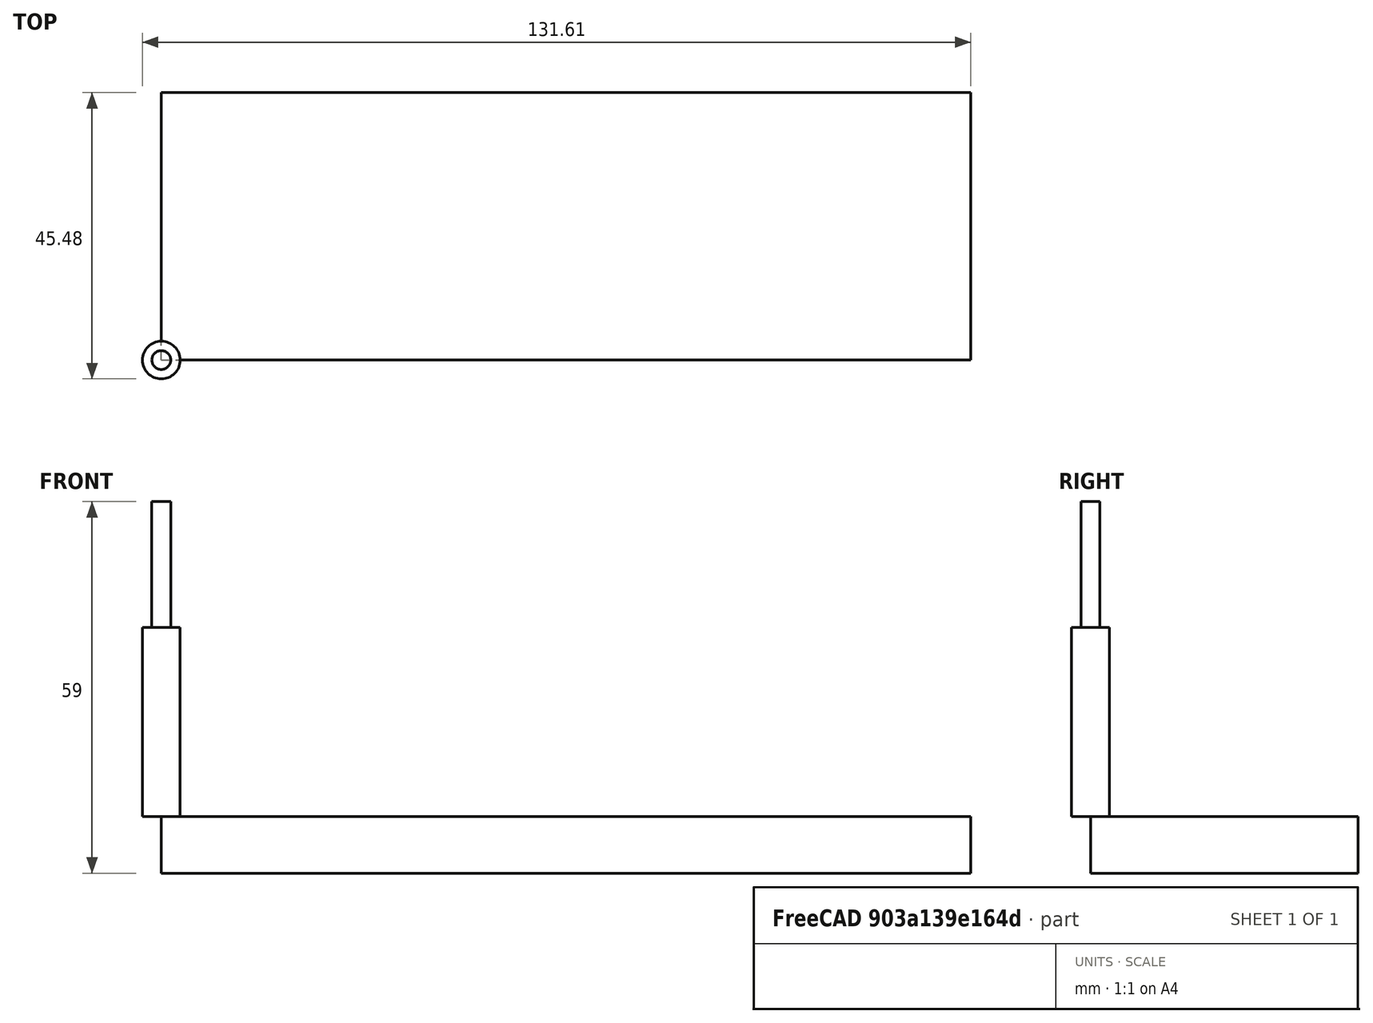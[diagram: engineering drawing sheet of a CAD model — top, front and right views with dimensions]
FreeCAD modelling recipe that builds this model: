
FCSTD DOCUMENT  (FreeCAD 0.19R24276 (Git))
Label: Coinceur2
License: All rights reserved
LicenseURL: http://en.wikipedia.org/wiki/All_rights_reserved
objects: Path::FeaturePython×5, Part::FeaturePython×3, App::DocumentObjectGroup×2, Sketcher::SketchObject×1, PartDesign::Pad×1, PartDesign::Body×1, App::FeaturePython×1, Path::FeatureCompoundPython×1, Mesh::FeaturePython×1
note: 9 computed .brp shape members not serialized (recipe doc carries the construction recipe); baked Part::Feature solids carry a one-line shape summary decoded from their .brp

FEATURE [Sketcher::SketchObject] Sketch002
  FullyConstrained = false
  sketch-geometry (712):
    g0: LineSegment StartX=49.1886 StartY=18.0693 StartZ=0 EndX=51.3408 EndY=18.9617 EndZ=0
    g1: LineSegment StartX=51.3408 StartY=18.9617 StartZ=0 EndX=57.8935 EndY=21.2147 EndZ=0
    g2: LineSegment StartX=57.8935 StartY=21.2147 StartZ=0 EndX=64.573 EndY=23.058 EndZ=0
    g3: LineSegment StartX=64.573 StartY=23.058 StartZ=0 EndX=71.3537 EndY=24.4846 EndZ=0
    g4: LineSegment StartX=71.3537 StartY=24.4846 StartZ=0 EndX=78.2097 EndY=25.4889 EndZ=0
    g5: LineSegment StartX=78.2097 StartY=25.4889 StartZ=0 EndX=85.1148 EndY=26.0672 EndZ=0
    g6: LineSegment StartX=85.1148 StartY=26.0672 StartZ=0 EndX=92.0423 EndY=26.2171 EndZ=0
    g7: LineSegment StartX=92.0423 StartY=26.2171 StartZ=0 EndX=98.9659 EndY=25.9383 EndZ=0
    g8: LineSegment StartX=98.9659 StartY=25.9383 StartZ=0 EndX=105.859 EndY=25.2316 EndZ=0
    g9: LineSegment StartX=105.859 StartY=25.2316 StartZ=0 EndX=112.695 EndY=24.0998 EndZ=0
    g10: LineSegment StartX=112.695 StartY=24.0998 StartZ=0 EndX=119.448 EndY=22.5473 EndZ=0
    g11: LineSegment StartX=119.448 StartY=22.5473 StartZ=0 EndX=126.092 EndY=20.5799 EndZ=0
    g12: LineSegment StartX=126.092 StartY=20.5799 StartZ=0 EndX=126.34 EndY=20.5026 EndZ=0
    g13: LineSegment StartX=126.34 StartY=20.5026 StartZ=0 EndX=126.59 EndY=20.4333 EndZ=0
    g14: LineSegment StartX=126.59 StartY=20.4333 StartZ=0 EndX=126.842 EndY=20.3722 EndZ=0
    g15: LineSegment StartX=126.842 StartY=20.3722 StartZ=0 EndX=127.096 EndY=20.3193 EndZ=0
    g16: LineSegment StartX=127.096 StartY=20.3193 StartZ=0 EndX=127.351 EndY=20.2746 EndZ=0
    g17: LineSegment StartX=127.351 StartY=20.2746 StartZ=0 EndX=127.608 EndY=20.2382 EndZ=0
    g18: LineSegment StartX=127.608 StartY=20.2382 StartZ=0 EndX=127.866 EndY=20.2102 EndZ=0
    g19: LineSegment StartX=127.866 StartY=20.2102 StartZ=0 EndX=128.125 EndY=20.1905 EndZ=0
    g20: LineSegment StartX=128.125 StartY=20.1905 StartZ=0 EndX=128.384 EndY=20.1793 EndZ=0
    g21: LineSegment StartX=128.384 StartY=20.1793 StartZ=0 EndX=128.643 EndY=20.1764 EndZ=0
    g22: LineSegment StartX=128.643 StartY=20.1764 StartZ=0 EndX=128.903 EndY=20.1819 EndZ=0
    g23: LineSegment StartX=128.903 StartY=20.1819 StartZ=0 EndX=129.162 EndY=20.1958 EndZ=0
    g24: LineSegment StartX=129.162 StartY=20.1958 StartZ=0 EndX=129.42 EndY=20.2181 EndZ=0
    g25: LineSegment StartX=129.42 StartY=20.2181 StartZ=0 EndX=129.678 EndY=20.2488 EndZ=0
    g26: LineSegment StartX=129.678 StartY=20.2488 StartZ=0 EndX=129.934 EndY=20.2877 EndZ=0
    g27: LineSegment StartX=129.934 StartY=20.2877 StartZ=0 EndX=130.189 EndY=20.335 EndZ=0
    g28: LineSegment StartX=130.189 StartY=20.335 StartZ=0 EndX=130.443 EndY=20.3905 EndZ=0
    g29: LineSegment StartX=130.443 StartY=20.3905 StartZ=0 EndX=130.694 EndY=20.4542 EndZ=0
    g30: LineSegment StartX=130.694 StartY=20.4542 StartZ=0 EndX=130.944 EndY=20.526 EndZ=0
    g31: LineSegment StartX=130.944 StartY=20.526 StartZ=0 EndX=131.191 EndY=20.6058 EndZ=0
    g32: LineSegment StartX=131.191 StartY=20.6058 StartZ=0 EndX=131.435 EndY=20.6936 EndZ=0
    g33: LineSegment StartX=131.435 StartY=20.6936 StartZ=0 EndX=131.676 EndY=20.7893 EndZ=0
    g34: LineSegment StartX=131.676 StartY=20.7893 StartZ=0 EndX=131.914 EndY=20.8927 EndZ=0
    g35: LineSegment StartX=131.914 StartY=20.8927 StartZ=0 EndX=132.148 EndY=21.0037 EndZ=0
    g36: LineSegment StartX=132.148 StartY=21.0037 StartZ=0 EndX=132.379 EndY=21.1223 EndZ=0
    g37: LineSegment StartX=132.379 StartY=21.1223 StartZ=0 EndX=132.606 EndY=21.2483 EndZ=0
    g38: LineSegment StartX=132.606 StartY=21.2483 StartZ=0 EndX=132.828 EndY=21.3816 EndZ=0
    g39: LineSegment StartX=132.828 StartY=21.3816 StartZ=0 EndX=133.046 EndY=21.522 EndZ=0
    g40: LineSegment StartX=133.046 StartY=21.522 StartZ=0 EndX=133.26 EndY=21.6694 EndZ=0
    g41: LineSegment StartX=133.26 StartY=21.6694 StartZ=0 EndX=133.469 EndY=21.8237 EndZ=0
    g42: LineSegment StartX=133.469 StartY=21.8237 StartZ=0 EndX=133.672 EndY=21.9846 EndZ=0
    g43: LineSegment StartX=133.672 StartY=21.9846 StartZ=0 EndX=133.87 EndY=22.152 EndZ=0
    g44: LineSegment StartX=133.87 StartY=22.152 StartZ=0 EndX=134.063 EndY=22.3258 EndZ=0
    g45: LineSegment StartX=134.063 StartY=22.3258 StartZ=0 EndX=134.25 EndY=22.5057 EndZ=0
    g46: LineSegment StartX=134.25 StartY=22.5057 StartZ=0 EndX=134.431 EndY=22.6915 EndZ=0
    g47: LineSegment StartX=134.431 StartY=22.6915 StartZ=0 EndX=134.606 EndY=22.8831 EndZ=0
    g48: LineSegment StartX=134.606 StartY=22.8831 StartZ=0 EndX=134.774 EndY=23.0803 EndZ=0
    g49: LineSegment StartX=134.774 StartY=23.0803 StartZ=0 EndX=134.936 EndY=23.2829 EndZ=0
    g50: LineSegment StartX=134.936 StartY=23.2829 StartZ=0 EndX=135.092 EndY=23.4906 EndZ=0
    g51: LineSegment StartX=135.092 StartY=23.4906 StartZ=0 EndX=135.24 EndY=23.7032 EndZ=0
    g52: LineSegment StartX=135.24 StartY=23.7032 StartZ=0 EndX=135.382 EndY=23.9205 EndZ=0
    g53: LineSegment StartX=135.382 StartY=23.9205 StartZ=0 EndX=135.517 EndY=24.1423 EndZ=0
    g54: LineSegment StartX=135.517 StartY=24.1423 StartZ=0 EndX=135.644 EndY=24.3683 EndZ=0
    g55: LineSegment StartX=135.644 StartY=24.3683 StartZ=0 EndX=135.764 EndY=24.5984 EndZ=0
    g56: LineSegment StartX=135.764 StartY=24.5984 StartZ=0 EndX=135.876 EndY=24.8322 EndZ=0
    g57: LineSegment StartX=135.876 StartY=24.8322 StartZ=0 EndX=135.981 EndY=25.0695 EndZ=0
    g58: LineSegment StartX=135.981 StartY=25.0695 StartZ=0 EndX=136.078 EndY=25.3101 EndZ=0
    g59: LineSegment StartX=136.078 StartY=25.3101 StartZ=0 EndX=136.167 EndY=25.5537 EndZ=0
    g60: LineSegment StartX=136.167 StartY=25.5537 StartZ=0 EndX=136.249 EndY=25.8001 EndZ=0
    g61: LineSegment StartX=136.249 StartY=25.8001 StartZ=0 EndX=136.322 EndY=26.0489 EndZ=0
    g62: LineSegment StartX=136.322 StartY=26.0489 StartZ=0 EndX=136.387 EndY=26.3 EndZ=0
    g63: LineSegment StartX=136.387 StartY=26.3 StartZ=0 EndX=136.444 EndY=26.5531 EndZ=0
    g64: LineSegment StartX=136.444 StartY=26.5531 StartZ=0 EndX=136.493 EndY=26.8079 EndZ=0
    g65: LineSegment StartX=136.493 StartY=26.8079 StartZ=0 EndX=136.533 EndY=27.0642 EndZ=0
    g66: LineSegment StartX=136.533 StartY=27.0642 StartZ=0 EndX=136.565 EndY=27.3216 EndZ=0
    g67: LineSegment StartX=136.565 StartY=27.3216 StartZ=0 EndX=136.589 EndY=27.5799 EndZ=0
    g68: LineSegment StartX=136.589 StartY=27.5799 StartZ=0 EndX=136.605 EndY=27.8389 EndZ=0
    g69: LineSegment StartX=136.605 StartY=27.8389 StartZ=0 EndX=136.612 EndY=28.0982 EndZ=0
    g70: LineSegment StartX=136.612 StartY=28.0982 StartZ=0 EndX=136.61 EndY=28.3577 EndZ=0
    g71: LineSegment StartX=136.61 StartY=28.3577 StartZ=0 EndX=136.601 EndY=28.6169 EndZ=0
    g72: LineSegment StartX=136.601 StartY=28.6169 StartZ=0 EndX=136.582 EndY=28.8757 EndZ=0
    g73: LineSegment StartX=136.582 StartY=28.8757 StartZ=0 EndX=136.556 EndY=29.1338 EndZ=0
    g74: LineSegment StartX=136.556 StartY=29.1338 StartZ=0 EndX=136.521 EndY=29.3908 EndZ=0
    g75: LineSegment StartX=136.521 StartY=29.3908 StartZ=0 EndX=136.478 EndY=29.6467 EndZ=0
    g76: LineSegment StartX=136.478 StartY=29.6467 StartZ=0 EndX=136.426 EndY=29.9009 EndZ=0
    g77: LineSegment StartX=136.426 StartY=29.9009 StartZ=0 EndX=136.367 EndY=30.1534 EndZ=0
    g78: LineSegment StartX=136.367 StartY=30.1534 StartZ=0 EndX=136.299 EndY=30.4038 EndZ=0
    g79: LineSegment StartX=136.299 StartY=30.4038 StartZ=0 EndX=136.223 EndY=30.6519 EndZ=0
    g80: LineSegment StartX=136.223 StartY=30.6519 StartZ=0 EndX=136.139 EndY=30.8974 EndZ=0
    g81: LineSegment StartX=136.139 StartY=30.8974 StartZ=0 EndX=136.048 EndY=31.1401 EndZ=0
    g82: LineSegment StartX=136.048 StartY=31.1401 StartZ=0 EndX=135.948 EndY=31.3796 EndZ=0
    g83: LineSegment StartX=135.948 StartY=31.3796 StartZ=0 EndX=135.841 EndY=31.6158 EndZ=0
    g84: LineSegment StartX=135.841 StartY=31.6158 StartZ=0 EndX=135.726 EndY=31.8484 EndZ=0
    g85: LineSegment StartX=135.726 StartY=31.8484 StartZ=0 EndX=135.603 EndY=32.0772 EndZ=0
    g86: LineSegment StartX=135.603 StartY=32.0772 StartZ=0 EndX=135.474 EndY=32.3019 EndZ=0
    g87: LineSegment StartX=135.474 StartY=32.3019 StartZ=0 EndX=135.337 EndY=32.5222 EndZ=0
    g88: LineSegment StartX=135.337 StartY=32.5222 StartZ=0 EndX=135.193 EndY=32.738 EndZ=0
    g89: LineSegment StartX=135.193 StartY=32.738 StartZ=0 EndX=135.042 EndY=32.9491 EndZ=0
    g90: LineSegment StartX=135.042 StartY=32.9491 StartZ=0 EndX=134.884 EndY=33.1551 EndZ=0
    g91: LineSegment StartX=134.884 StartY=33.1551 StartZ=0 EndX=134.72 EndY=33.3559 EndZ=0
    g92: LineSegment StartX=134.72 StartY=33.3559 StartZ=0 EndX=134.549 EndY=33.5513 EndZ=0
    g93: LineSegment StartX=134.549 StartY=33.5513 StartZ=0 EndX=134.373 EndY=33.7411 EndZ=0
    g94: LineSegment StartX=134.373 StartY=33.7411 StartZ=0 EndX=134.19 EndY=33.9251 EndZ=0
    g95: LineSegment StartX=134.19 StartY=33.9251 StartZ=0 EndX=134.001 EndY=34.103 EndZ=0
    g96: LineSegment StartX=134.001 StartY=34.103 StartZ=0 EndX=133.806 EndY=34.2747 EndZ=0
    g97: LineSegment StartX=133.806 StartY=34.2747 StartZ=0 EndX=133.606 EndY=34.44 EndZ=0
    g98: LineSegment StartX=133.606 StartY=34.44 StartZ=0 EndX=133.401 EndY=34.5988 EndZ=0
    g99: LineSegment StartX=133.401 StartY=34.5988 StartZ=0 EndX=133.191 EndY=34.7508 EndZ=0
    g100: LineSegment StartX=133.191 StartY=34.7508 StartZ=0 EndX=132.976 EndY=34.896 EndZ=0
    g101: LineSegment StartX=132.976 StartY=34.896 StartZ=0 EndX=132.756 EndY=35.0341 EndZ=0
    g102: LineSegment StartX=132.756 StartY=35.0341 StartZ=0 EndX=132.532 EndY=35.165 EndZ=0
    g103: LineSegment StartX=132.532 StartY=35.165 StartZ=0 EndX=132.304 EndY=35.2886 EndZ=0
    g104: LineSegment StartX=132.304 StartY=35.2886 StartZ=0 EndX=132.072 EndY=35.4048 EndZ=0
    g105: LineSegment StartX=132.072 StartY=35.4048 StartZ=0 EndX=131.837 EndY=35.5134 EndZ=0
    g106: LineSegment StartX=131.837 StartY=35.5134 StartZ=0 EndX=131.598 EndY=35.6143 EndZ=0
    g107: LineSegment StartX=131.598 StartY=35.6143 StartZ=0 EndX=131.356 EndY=35.7074 EndZ=0
    g108: LineSegment StartX=131.356 StartY=35.7074 StartZ=0 EndX=131.111 EndY=35.7926 EndZ=0
    g109: LineSegment StartX=131.111 StartY=35.7926 StartZ=0 EndX=130.863 EndY=35.8698 EndZ=0
    g110: LineSegment StartX=130.863 StartY=35.8698 StartZ=0 EndX=130.613 EndY=36 EndZ=0
    g111: LineSegment StartX=130.613 StartY=36 StartZ=0 EndX=130.361 EndY=36 EndZ=0
    g112: LineSegment StartX=130.361 StartY=36 StartZ=0 EndX=129.386 EndY=36.2768 EndZ=0
    g113: LineSegment StartX=129.386 StartY=36.2768 StartZ=0 EndX=128.411 EndY=36.551 EndZ=0
    g114: LineSegment StartX=128.411 StartY=36.551 StartZ=0 EndX=127.435 EndY=36.8224 EndZ=0
    g115: LineSegment StartX=127.435 StartY=36.8224 StartZ=0 EndX=126.458 EndY=37.0911 EndZ=0
    g116: LineSegment StartX=126.458 StartY=37.0911 StartZ=0 EndX=125.481 EndY=37.357 EndZ=0
    g117: LineSegment StartX=125.481 StartY=37.357 StartZ=0 EndX=124.503 EndY=37.6203 EndZ=0
    g118: LineSegment StartX=124.503 StartY=37.6203 StartZ=0 EndX=123.524 EndY=37.8808 EndZ=0
    g119: LineSegment StartX=123.524 StartY=37.8808 StartZ=0 EndX=122.544 EndY=38.1386 EndZ=0
    g120: LineSegment StartX=122.544 StartY=38.1386 StartZ=0 EndX=121.564 EndY=38.3937 EndZ=0
    g121: LineSegment StartX=121.564 StartY=38.3937 StartZ=0 EndX=120.583 EndY=38.6461 EndZ=0
    g122: LineSegment StartX=120.583 StartY=38.6461 StartZ=0 EndX=119.601 EndY=38.8957 EndZ=0
    g123: LineSegment StartX=119.601 StartY=38.8957 StartZ=0 EndX=118.618 EndY=39.1426 EndZ=0
    g124: LineSegment StartX=118.618 StartY=39.1426 StartZ=0 EndX=117.635 EndY=39.3868 EndZ=0
    g125: LineSegment StartX=117.635 StartY=39.3868 StartZ=0 EndX=116.651 EndY=39.6282 EndZ=0
    g126: LineSegment StartX=116.651 StartY=39.6282 StartZ=0 EndX=115.667 EndY=39.8669 EndZ=0
    g127: LineSegment StartX=115.667 StartY=39.8669 StartZ=0 EndX=114.682 EndY=40.1028 EndZ=0
    g128: LineSegment StartX=114.682 StartY=40.1028 StartZ=0 EndX=113.696 EndY=40.336 EndZ=0
    g129: LineSegment StartX=113.696 StartY=40.336 StartZ=0 EndX=112.709 EndY=40.5665 EndZ=0
    g130: LineSegment StartX=112.709 StartY=40.5665 StartZ=0 EndX=111.722 EndY=40.7942 EndZ=0
    g131: LineSegment StartX=111.722 StartY=40.7942 StartZ=0 EndX=110.735 EndY=41.0192 EndZ=0
    g132: LineSegment StartX=110.735 StartY=41.0192 StartZ=0 EndX=109.746 EndY=41.2414 EndZ=0
    g133: LineSegment StartX=109.746 StartY=41.2414 StartZ=0 EndX=108.757 EndY=41.4608 EndZ=0
    g134: LineSegment StartX=108.757 StartY=41.4608 StartZ=0 EndX=107.768 EndY=41.6776 EndZ=0
    g135: LineSegment StartX=107.768 StartY=41.6776 StartZ=0 EndX=106.778 EndY=41.8915 EndZ=0
    g136: LineSegment StartX=106.778 StartY=41.8915 StartZ=0 EndX=105.787 EndY=42.1027 EndZ=0
    g137: LineSegment StartX=105.787 StartY=42.1027 StartZ=0 EndX=104.796 EndY=42.3112 EndZ=0
    g138: LineSegment StartX=104.796 StartY=42.3112 StartZ=0 EndX=103.804 EndY=42.5169 EndZ=0
    g139: LineSegment StartX=103.804 StartY=42.5169 StartZ=0 EndX=102.811 EndY=42.7198 EndZ=0
    g140: LineSegment StartX=102.811 StartY=42.7198 StartZ=0 EndX=101.818 EndY=42.92 EndZ=0
    g141: LineSegment StartX=101.818 StartY=42.92 StartZ=0 EndX=100.825 EndY=43.1174 EndZ=0
    g142: LineSegment StartX=100.825 StartY=43.1174 StartZ=0 EndX=99.8304 EndY=43.312 EndZ=0
    g143: LineSegment StartX=99.8304 StartY=43.312 StartZ=0 EndX=98.8357 EndY=43.5039 EndZ=0
    g144: LineSegment StartX=98.8357 StartY=43.5039 StartZ=0 EndX=97.8405 EndY=43.693 EndZ=0
    g145: LineSegment StartX=97.8405 StartY=43.693 StartZ=0 EndX=96.8448 EndY=43.8793 EndZ=0
    g146: LineSegment StartX=96.8448 StartY=43.8793 StartZ=0 EndX=95.8485 EndY=44.0629 EndZ=0
    g147: LineSegment StartX=95.8485 StartY=44.0629 StartZ=0 EndX=94.8518 EndY=44.2437 EndZ=0
    g148: LineSegment StartX=94.8518 StartY=44.2437 StartZ=0 EndX=93.8545 EndY=44.4217 EndZ=0
    g149: LineSegment StartX=93.8545 StartY=44.4217 StartZ=0 EndX=92.8568 EndY=44.597 EndZ=0
    g150: LineSegment StartX=92.8568 StartY=44.597 StartZ=0 EndX=91.8585 EndY=44.7694 EndZ=0
    g151: LineSegment StartX=91.8585 StartY=44.7694 StartZ=0 EndX=90.8598 EndY=44.9391 EndZ=0
    g152: LineSegment StartX=90.8598 StartY=44.9391 StartZ=0 EndX=89.8607 EndY=45.1061 EndZ=0
    g153: LineSegment StartX=89.8607 StartY=45.1061 StartZ=0 EndX=88.861 EndY=45.2702 EndZ=0
    g154: LineSegment StartX=88.861 StartY=45.2702 StartZ=0 EndX=87.861 EndY=45.4315 EndZ=0
    g155: LineSegment StartX=87.861 StartY=45.4315 StartZ=0 EndX=86.8604 EndY=45.5901 EndZ=0
    g156: LineSegment StartX=86.8604 StartY=45.5901 StartZ=0 EndX=85.8595 EndY=45.7459 EndZ=0
    g157: LineSegment StartX=85.8595 StartY=45.7459 StartZ=0 EndX=84.8581 EndY=45.8989 EndZ=0
    g158: LineSegment StartX=84.8581 StartY=45.8989 StartZ=0 EndX=83.8563 EndY=46.0491 EndZ=0
    g159: LineSegment StartX=83.8563 StartY=46.0491 StartZ=0 EndX=82.854 EndY=46.1965 EndZ=0
    g160: LineSegment StartX=82.854 StartY=46.1965 StartZ=0 EndX=81.8514 EndY=46.3412 EndZ=0
    g161: LineSegment StartX=81.8514 StartY=46.3412 StartZ=0 EndX=80.8483 EndY=46.483 EndZ=0
    g162: LineSegment StartX=80.8483 StartY=46.483 StartZ=0 EndX=79.8449 EndY=46.6221 EndZ=0
    g163: LineSegment StartX=79.8449 StartY=46.6221 StartZ=0 EndX=78.8411 EndY=46.7583 EndZ=0
    g164: LineSegment StartX=78.8411 StartY=46.7583 StartZ=0 EndX=77.8369 EndY=46.8918 EndZ=0
    g165: LineSegment StartX=77.8369 StartY=46.8918 StartZ=0 EndX=76.8324 EndY=47.0225 EndZ=0
    g166: LineSegment StartX=76.8324 StartY=47.0225 StartZ=0 EndX=75.8275 EndY=47.1504 EndZ=0
    g167: LineSegment StartX=75.8275 StartY=47.1504 StartZ=0 EndX=74.8222 EndY=47.2755 EndZ=0
    g168: LineSegment StartX=74.8222 StartY=47.2755 StartZ=0 EndX=73.8166 EndY=47.3977 EndZ=0
    g169: LineSegment StartX=73.8166 StartY=47.3977 StartZ=0 EndX=72.8107 EndY=47.5172 EndZ=0
    g170: LineSegment StartX=72.8107 StartY=47.5172 StartZ=0 EndX=71.8044 EndY=47.6339 EndZ=0
    g171: LineSegment StartX=71.8044 StartY=47.6339 StartZ=0 EndX=70.7978 EndY=47.7478 EndZ=0
    g172: LineSegment StartX=70.7978 StartY=47.7478 StartZ=0 EndX=69.7909 EndY=47.8589 EndZ=0
    g173: LineSegment StartX=69.7909 StartY=47.8589 StartZ=0 EndX=68.7837 EndY=47.9672 EndZ=0
    g174: LineSegment StartX=68.7837 StartY=47.9672 StartZ=0 EndX=67.7762 EndY=48.0727 EndZ=0
    g175: LineSegment StartX=67.7762 StartY=48.0727 StartZ=0 EndX=66.7684 EndY=48.1754 EndZ=0
    g176: LineSegment StartX=66.7684 StartY=48.1754 StartZ=0 EndX=65.7603 EndY=48.2753 EndZ=0
    g177: LineSegment StartX=65.7603 StartY=48.2753 StartZ=0 EndX=64.7519 EndY=48.3723 EndZ=0
    g178: LineSegment StartX=64.7519 StartY=48.3723 StartZ=0 EndX=63.7433 EndY=48.4666 EndZ=0
    g179: LineSegment StartX=63.7433 StartY=48.4666 StartZ=0 EndX=62.7344 EndY=48.5581 EndZ=0
    g180: LineSegment StartX=62.7344 StartY=48.5581 StartZ=0 EndX=61.7253 EndY=48.6467 EndZ=0
    g181: LineSegment StartX=61.7253 StartY=48.6467 StartZ=0 EndX=60.7159 EndY=48.7326 EndZ=0
    g182: LineSegment StartX=60.7159 StartY=48.7326 StartZ=0 EndX=59.7063 EndY=48.8156 EndZ=0
    g183: LineSegment StartX=59.7063 StartY=48.8156 StartZ=0 EndX=58.6965 EndY=48.8959 EndZ=0
    g184: LineSegment StartX=58.6965 StartY=48.8959 StartZ=0 EndX=57.6864 EndY=48.9733 EndZ=0
    g185: LineSegment StartX=57.6864 StartY=48.9733 StartZ=0 EndX=56.6762 EndY=49.0479 EndZ=0
    g186: LineSegment StartX=56.6762 StartY=49.0479 StartZ=0 EndX=55.6657 EndY=49.1197 EndZ=0
    g187: LineSegment StartX=55.6657 StartY=49.1197 StartZ=0 EndX=54.655 EndY=49.1887 EndZ=0
    g188: LineSegment StartX=54.655 StartY=49.1887 StartZ=0 EndX=53.6442 EndY=49.2549 EndZ=0
    g189: LineSegment StartX=53.6442 StartY=49.2549 StartZ=0 EndX=52.6332 EndY=49.3182 EndZ=0
    g190: LineSegment StartX=52.6332 StartY=49.3182 StartZ=0 EndX=51.622 EndY=49.3788 EndZ=0
    g191: LineSegment StartX=51.622 StartY=49.3788 StartZ=0 EndX=50.6106 EndY=49.4365 EndZ=0
    g192: LineSegment StartX=50.6106 StartY=49.4365 StartZ=0 EndX=49.5991 EndY=49.4914 EndZ=0
    g193: LineSegment StartX=49.5991 StartY=49.4914 StartZ=0 EndX=48.5874 EndY=49.5436 EndZ=0
    g194: LineSegment StartX=48.5874 StartY=49.5436 StartZ=0 EndX=47.5756 EndY=49.5929 EndZ=0
    g195: LineSegment StartX=47.5756 StartY=49.5929 StartZ=0 EndX=46.5636 EndY=49.6393 EndZ=0
    g196: LineSegment StartX=46.5636 StartY=49.6393 StartZ=0 EndX=45.5516 EndY=49.683 EndZ=0
    g197: LineSegment StartX=45.5516 StartY=49.683 StartZ=0 EndX=44.5394 EndY=49.7239 EndZ=0
    g198: LineSegment StartX=44.5394 StartY=49.7239 StartZ=0 EndX=43.5271 EndY=49.7619 EndZ=0
    g199: LineSegment StartX=43.5271 StartY=49.7619 StartZ=0 EndX=42.5147 EndY=49.7971 EndZ=0
    g200: LineSegment StartX=42.5147 StartY=49.7971 StartZ=0 EndX=41.5022 EndY=49.8295 EndZ=0
    g201: LineSegment StartX=41.5022 StartY=49.8295 StartZ=0 EndX=40.4896 EndY=49.8591 EndZ=0
    g202: LineSegment StartX=40.4896 StartY=49.8591 StartZ=0 EndX=39.4769 EndY=49.8859 EndZ=0
    g203: LineSegment StartX=39.4769 StartY=49.8859 StartZ=0 EndX=38.4642 EndY=49.9098 EndZ=0
    g204: LineSegment StartX=38.4642 StartY=49.9098 StartZ=0 EndX=37.4514 EndY=49.931 EndZ=0
    g205: LineSegment StartX=37.4514 StartY=49.931 StartZ=0 EndX=36.4385 EndY=49.9493 EndZ=0
    g206: LineSegment StartX=36.4385 StartY=49.9493 StartZ=0 EndX=35.4256 EndY=49.9648 EndZ=0
    g207: LineSegment StartX=35.4256 StartY=49.9648 StartZ=0 EndX=34.4127 EndY=49.9775 EndZ=0
    g208: LineSegment StartX=34.4127 StartY=49.9775 StartZ=0 EndX=33.3997 EndY=49.9873 EndZ=0
    g209: LineSegment StartX=33.3997 StartY=49.9873 StartZ=0 EndX=32.3867 EndY=49.9944 EndZ=0
    g210: LineSegment StartX=32.3867 StartY=49.9944 StartZ=0 EndX=30.3607 EndY=49.9895 EndZ=0
    g211: LineSegment StartX=30.3607 StartY=49.9895 StartZ=0 EndX=30.2393 EndY=50.0208 EndZ=0
    g212: LineSegment StartX=30.2393 StartY=50.0208 StartZ=0 EndX=30.1176 EndY=50.0511 EndZ=0
    g213: LineSegment StartX=30.1176 StartY=50.0511 StartZ=0 EndX=29.9957 EndY=50.0804 EndZ=0
    g214: LineSegment StartX=29.9957 StartY=50.0804 StartZ=0 EndX=29.8735 EndY=50.1087 EndZ=0
    g215: LineSegment StartX=29.8735 StartY=50.1087 StartZ=0 EndX=29.7511 EndY=50.1359 EndZ=0
    g216: LineSegment StartX=29.7511 StartY=50.1359 StartZ=0 EndX=29.6284 EndY=50.1621 EndZ=0
    g217: LineSegment StartX=29.6284 StartY=50.1621 StartZ=0 EndX=29.5056 EndY=50.1873 EndZ=0
    g218: LineSegment StartX=29.5056 StartY=50.1873 StartZ=0 EndX=29.3825 EndY=50.2114 EndZ=0
    g219: LineSegment StartX=29.3825 StartY=50.2114 StartZ=0 EndX=29.2593 EndY=50.2345 EndZ=0
    g220: LineSegment StartX=29.2593 StartY=50.2345 StartZ=0 EndX=29.1359 EndY=50.2566 EndZ=0
    g221: LineSegment StartX=29.1359 StartY=50.2566 StartZ=0 EndX=29.0122 EndY=50.2777 EndZ=0
    g222: LineSegment StartX=29.0122 StartY=50.2777 StartZ=0 EndX=28.8884 EndY=50.2977 EndZ=0
    g223: LineSegment StartX=28.8884 StartY=50.2977 StartZ=0 EndX=28.7645 EndY=50.3167 EndZ=0
    g224: LineSegment StartX=28.7645 StartY=50.3167 StartZ=0 EndX=28.6404 EndY=50.3346 EndZ=0
    g225: LineSegment StartX=28.6404 StartY=50.3346 StartZ=0 EndX=28.5161 EndY=50.3516 EndZ=0
    g226: LineSegment StartX=28.5161 StartY=50.3516 StartZ=0 EndX=28.3917 EndY=50.3674 EndZ=0
    g227: LineSegment StartX=28.3917 StartY=50.3674 StartZ=0 EndX=28.2672 EndY=50.3823 EndZ=0
    g228: LineSegment StartX=28.2672 StartY=50.3823 StartZ=0 EndX=28.1426 EndY=50.396 EndZ=0
    g229: LineSegment StartX=28.1426 StartY=50.396 StartZ=0 EndX=28.0178 EndY=50.4088 EndZ=0
    g230: LineSegment StartX=28.0178 StartY=50.4088 StartZ=0 EndX=27.893 EndY=50.4205 EndZ=0
    g231: LineSegment StartX=27.893 StartY=50.4205 StartZ=0 EndX=27.768 EndY=50.4312 EndZ=0
    g232: LineSegment StartX=27.768 StartY=50.4312 StartZ=0 EndX=27.643 EndY=50.4408 EndZ=0
    g233: LineSegment StartX=27.643 StartY=50.4408 StartZ=0 EndX=27.5179 EndY=50.4493 EndZ=0
    g234: LineSegment StartX=27.5179 StartY=50.4493 StartZ=0 EndX=27.3927 EndY=50.4569 EndZ=0
    g235: LineSegment StartX=27.3927 StartY=50.4569 StartZ=0 EndX=27.2675 EndY=50.4633 EndZ=0
    g236: LineSegment StartX=27.2675 StartY=50.4633 StartZ=0 EndX=27.1422 EndY=50.4688 EndZ=0
    g237: LineSegment StartX=27.1422 StartY=50.4688 StartZ=0 EndX=27.0169 EndY=50.4732 EndZ=0
    g238: LineSegment StartX=27.0169 StartY=50.4732 StartZ=0 EndX=26.8915 EndY=50.4765 EndZ=0
    g239: LineSegment StartX=26.8915 StartY=50.4765 StartZ=0 EndX=26.7661 EndY=50.4788 EndZ=0
    g240: LineSegment StartX=26.7661 StartY=50.4788 StartZ=0 EndX=26.6407 EndY=50.48 EndZ=0
    g241: LineSegment StartX=26.6407 StartY=50.48 StartZ=0 EndX=26.5153 EndY=50.4802 EndZ=0
    g242: LineSegment StartX=26.5153 StartY=50.4802 StartZ=0 EndX=26.3899 EndY=50.4793 EndZ=0
    g243: LineSegment StartX=26.3899 StartY=50.4793 StartZ=0 EndX=26.2645 EndY=50.4774 EndZ=0
    g244: LineSegment StartX=26.2645 StartY=50.4774 StartZ=0 EndX=26.1392 EndY=50.4745 EndZ=0
    g245: LineSegment StartX=26.1392 StartY=50.4745 StartZ=0 EndX=26.0138 EndY=50.4705 EndZ=0
    g246: LineSegment StartX=26.0138 StartY=50.4705 StartZ=0 EndX=25.8885 EndY=50.4654 EndZ=0
    g247: LineSegment StartX=25.8885 StartY=50.4654 StartZ=0 EndX=25.7633 EndY=50.4593 EndZ=0
    g248: LineSegment StartX=25.7633 StartY=50.4593 StartZ=0 EndX=25.6381 EndY=50.4522 EndZ=0
    g249: LineSegment StartX=25.6381 StartY=50.4522 StartZ=0 EndX=25.5129 EndY=50.444 EndZ=0
    g250: LineSegment StartX=25.5129 StartY=50.444 StartZ=0 EndX=25.3879 EndY=50.4348 EndZ=0
    g251: LineSegment StartX=25.3879 StartY=50.4348 StartZ=0 EndX=25.2629 EndY=50.4245 EndZ=0
    g252: LineSegment StartX=25.2629 StartY=50.4245 StartZ=0 EndX=25.138 EndY=50.4131 EndZ=0
    g253: LineSegment StartX=25.138 StartY=50.4131 StartZ=0 EndX=25.0132 EndY=50.4008 EndZ=0
    g254: LineSegment StartX=25.0132 StartY=50.4008 StartZ=0 EndX=24.8885 EndY=50.3874 EndZ=0
    g255: LineSegment StartX=24.8885 StartY=50.3874 StartZ=0 EndX=24.764 EndY=50.3729 EndZ=0
    g256: LineSegment StartX=24.764 StartY=50.3729 StartZ=0 EndX=24.6395 EndY=50.3574 EndZ=0
    g257: LineSegment StartX=24.6395 StartY=50.3574 StartZ=0 EndX=24.5152 EndY=50.3409 EndZ=0
    g258: LineSegment StartX=24.5152 StartY=50.3409 StartZ=0 EndX=24.3911 EndY=50.3233 EndZ=0
    g259: LineSegment StartX=24.3911 StartY=50.3233 StartZ=0 EndX=24.2671 EndY=50.3047 EndZ=0
    g260: LineSegment StartX=24.2671 StartY=50.3047 StartZ=0 EndX=24.1432 EndY=50.285 EndZ=0
    g261: LineSegment StartX=24.1432 StartY=50.285 StartZ=0 EndX=24.0195 EndY=50.2644 EndZ=0
    g262: LineSegment StartX=24.0195 StartY=50.2644 StartZ=0 EndX=23.896 EndY=50.2426 EndZ=0
    g263: LineSegment StartX=23.896 StartY=50.2426 StartZ=0 EndX=23.7727 EndY=50.2199 EndZ=0
    g264: LineSegment StartX=23.7727 StartY=50.2199 StartZ=0 EndX=23.6496 EndY=50.1961 EndZ=0
    g265: LineSegment StartX=23.6496 StartY=50.1961 StartZ=0 EndX=23.5266 EndY=50.1713 EndZ=0
    g266: LineSegment StartX=23.5266 StartY=50.1713 StartZ=0 EndX=23.4039 EndY=50.1455 EndZ=0
    g267: LineSegment StartX=23.4039 StartY=50.1455 StartZ=0 EndX=23.2814 EndY=50.1186 EndZ=0
    g268: LineSegment StartX=23.2814 StartY=50.1186 StartZ=0 EndX=23.1592 EndY=50.0907 EndZ=0
    g269: LineSegment StartX=23.1592 StartY=50.0907 StartZ=0 EndX=23.0371 EndY=50.0618 EndZ=0
    g270: LineSegment StartX=23.0371 StartY=50.0618 StartZ=0 EndX=22.9154 EndY=50.0319 EndZ=0
    g271: LineSegment StartX=22.9154 StartY=50.0319 StartZ=0 EndX=22.7938 EndY=50.001 EndZ=0
    g272: LineSegment StartX=22.7938 StartY=50.001 StartZ=0 EndX=22.6726 EndY=49.969 EndZ=0
    g273: LineSegment StartX=22.6726 StartY=49.969 StartZ=0 EndX=22.5516 EndY=49.9361 EndZ=0
    g274: LineSegment StartX=22.5516 StartY=49.9361 StartZ=0 EndX=22.4309 EndY=49.9021 EndZ=0
    g275: LineSegment StartX=22.4309 StartY=49.9021 StartZ=0 EndX=22.3105 EndY=49.8671 EndZ=0
    g276: LineSegment StartX=22.3105 StartY=49.8671 StartZ=0 EndX=22.1903 EndY=49.8311 EndZ=0
    g277: LineSegment StartX=22.1903 StartY=49.8311 StartZ=0 EndX=22.0705 EndY=49.7941 EndZ=0
    g278: LineSegment StartX=22.0705 StartY=49.7941 StartZ=0 EndX=21.951 EndY=49.7561 EndZ=0
    g279: LineSegment StartX=21.951 StartY=49.7561 StartZ=0 EndX=21.8318 EndY=49.7171 EndZ=0
    g280: LineSegment StartX=21.8318 StartY=49.7171 StartZ=0 EndX=21.713 EndY=49.6771 EndZ=0
    g281: LineSegment StartX=21.713 StartY=49.6771 StartZ=0 EndX=21.5944 EndY=49.6362 EndZ=0
    g282: LineSegment StartX=21.5944 StartY=49.6362 StartZ=0 EndX=21.4763 EndY=49.5942 EndZ=0
    g283: LineSegment StartX=21.4763 StartY=49.5942 StartZ=0 EndX=21.3585 EndY=49.5512 EndZ=0
    g284: LineSegment StartX=21.3585 StartY=49.5512 StartZ=0 EndX=21.241 EndY=49.5073 EndZ=0
    g285: LineSegment StartX=21.241 StartY=49.5073 StartZ=0 EndX=21.1239 EndY=49.4624 EndZ=0
    g286: LineSegment StartX=21.1239 StartY=49.4624 StartZ=0 EndX=21.0072 EndY=49.4165 EndZ=0
    g287: LineSegment StartX=21.0072 StartY=49.4165 StartZ=0 EndX=20.8909 EndY=49.3696 EndZ=0
    g288: LineSegment StartX=20.8909 StartY=49.3696 StartZ=0 EndX=20.775 EndY=49.3218 EndZ=0
    g289: LineSegment StartX=20.775 StartY=49.3218 StartZ=0 EndX=20.6595 EndY=49.273 EndZ=0
    g290: LineSegment StartX=20.6595 StartY=49.273 StartZ=0 EndX=20.5444 EndY=49.2232 EndZ=0
    g291: LineSegment StartX=20.5444 StartY=49.2232 StartZ=0 EndX=20.4297 EndY=49.1725 EndZ=0
    g292: LineSegment StartX=20.4297 StartY=49.1725 StartZ=0 EndX=20.3154 EndY=49.1208 EndZ=0
    g293: LineSegment StartX=20.3154 StartY=49.1208 StartZ=0 EndX=20.2016 EndY=49.0681 EndZ=0
    g294: LineSegment StartX=20.2016 StartY=49.0681 StartZ=0 EndX=20.0883 EndY=49.0145 EndZ=0
    g295: LineSegment StartX=20.0883 StartY=49.0145 StartZ=0 EndX=19.9753 EndY=48.96 EndZ=0
    g296: LineSegment StartX=19.9753 StartY=48.96 StartZ=0 EndX=19.8629 EndY=48.9045 EndZ=0
    g297: LineSegment StartX=19.8629 StartY=48.9045 StartZ=0 EndX=19.7509 EndY=48.8481 EndZ=0
    g298: LineSegment StartX=19.7509 StartY=48.8481 StartZ=0 EndX=19.6394 EndY=48.7907 EndZ=0
    g299: LineSegment StartX=19.6394 StartY=48.7907 StartZ=0 EndX=19.5283 EndY=48.7325 EndZ=0
    g300: LineSegment StartX=19.5283 StartY=48.7325 StartZ=0 EndX=19.4178 EndY=48.6733 EndZ=0
    g301: LineSegment StartX=19.4178 StartY=48.6733 StartZ=0 EndX=19.3077 EndY=48.6131 EndZ=0
    g302: LineSegment StartX=19.3077 StartY=48.6131 StartZ=0 EndX=19.1982 EndY=48.5521 EndZ=0
    g303: LineSegment StartX=19.1982 StartY=48.5521 StartZ=0 EndX=19.0892 EndY=48.4901 EndZ=0
    g304: LineSegment StartX=19.0892 StartY=48.4901 StartZ=0 EndX=18.9807 EndY=48.4272 EndZ=0
    g305: LineSegment StartX=18.9807 StartY=48.4272 StartZ=0 EndX=18.8727 EndY=48.3635 EndZ=0
    g306: LineSegment StartX=18.8727 StartY=48.3635 StartZ=0 EndX=18.7653 EndY=48.2988 EndZ=0
    g307: LineSegment StartX=18.7653 StartY=48.2988 StartZ=0 EndX=18.6584 EndY=48.2332 EndZ=0
    g308: LineSegment StartX=18.6584 StartY=48.2332 StartZ=0 EndX=18.552 EndY=48.1667 EndZ=0
    g309: LineSegment StartX=18.552 StartY=48.1667 StartZ=0 EndX=18.4463 EndY=48.0994 EndZ=0
    g310: LineSegment StartX=18.4463 StartY=48.0994 StartZ=0 EndX=18.341 EndY=48.0312 EndZ=0
    g311: LineSegment StartX=18.341 StartY=48.0312 StartZ=0 EndX=18.2164 EndY=47.9503 EndZ=0
    g312: LineSegment StartX=18.2164 StartY=47.9503 StartZ=0 EndX=18.0924 EndY=47.8684 EndZ=0
    g313: LineSegment StartX=18.0924 StartY=47.8684 StartZ=0 EndX=17.9691 EndY=47.7855 EndZ=0
    g314: LineSegment StartX=17.9691 StartY=47.7855 StartZ=0 EndX=17.8464 EndY=47.7016 EndZ=0
    g315: LineSegment StartX=17.8464 StartY=47.7016 StartZ=0 EndX=17.7245 EndY=47.6166 EndZ=0
    g316: LineSegment StartX=17.7245 StartY=47.6166 StartZ=0 EndX=17.6033 EndY=47.5307 EndZ=0
    g317: LineSegment StartX=17.6033 StartY=47.5307 StartZ=0 EndX=17.4828 EndY=47.4438 EndZ=0
    g318: LineSegment StartX=17.4828 StartY=47.4438 StartZ=0 EndX=17.363 EndY=47.3558 EndZ=0
    g319: LineSegment StartX=17.363 StartY=47.3558 StartZ=0 EndX=17.2439 EndY=47.2669 EndZ=0
    g320: LineSegment StartX=17.2439 StartY=47.2669 StartZ=0 EndX=17.1256 EndY=47.177 EndZ=0
    g321: LineSegment StartX=17.1256 StartY=47.177 StartZ=0 EndX=17.008 EndY=47.0862 EndZ=0
    g322: LineSegment StartX=17.008 StartY=47.0862 StartZ=0 EndX=16.8912 EndY=46.9943 EndZ=0
    g323: LineSegment StartX=16.8912 StartY=46.9943 StartZ=0 EndX=16.7751 EndY=46.9015 EndZ=0
    g324: LineSegment StartX=16.7751 StartY=46.9015 StartZ=0 EndX=16.6599 EndY=46.8078 EndZ=0
    g325: LineSegment StartX=16.6599 StartY=46.8078 StartZ=0 EndX=16.5453 EndY=46.7131 EndZ=0
    g326: LineSegment StartX=16.5453 StartY=46.7131 StartZ=0 EndX=16.4316 EndY=46.6174 EndZ=0
    g327: LineSegment StartX=16.4316 StartY=46.6174 StartZ=0 EndX=16.3187 EndY=46.5208 EndZ=0
    g328: LineSegment StartX=16.3187 StartY=46.5208 StartZ=0 EndX=16.2066 EndY=46.4233 EndZ=0
    g329: LineSegment StartX=16.2066 StartY=46.4233 StartZ=0 EndX=16.0952 EndY=46.3249 EndZ=0
    g330: LineSegment StartX=16.0952 StartY=46.3249 StartZ=0 EndX=15.9847 EndY=46.2256 EndZ=0
    g331: LineSegment StartX=15.9847 StartY=46.2256 StartZ=0 EndX=15.875 EndY=46.1253 EndZ=0
    g332: LineSegment StartX=15.875 StartY=46.1253 StartZ=0 EndX=15.7662 EndY=46.0241 EndZ=0
    g333: LineSegment StartX=15.7662 StartY=46.0241 StartZ=0 EndX=15.6582 EndY=45.9221 EndZ=0
    g334: LineSegment StartX=15.6582 StartY=45.9221 StartZ=0 EndX=15.551 EndY=45.8192 EndZ=0
    g335: LineSegment StartX=15.551 StartY=45.8192 StartZ=0 EndX=15.4447 EndY=45.7153 EndZ=0
    g336: LineSegment StartX=15.4447 StartY=45.7153 StartZ=0 EndX=15.3393 EndY=45.6106 EndZ=0
    g337: LineSegment StartX=15.3393 StartY=45.6106 StartZ=0 EndX=15.2347 EndY=45.5051 EndZ=0
    g338: LineSegment StartX=15.2347 StartY=45.5051 StartZ=0 EndX=15.131 EndY=45.3987 EndZ=0
    g339: LineSegment StartX=15.131 StartY=45.3987 StartZ=0 EndX=15.0281 EndY=45.2914 EndZ=0
    g340: LineSegment StartX=15.0281 StartY=45.2914 StartZ=0 EndX=14.9262 EndY=45.1833 EndZ=0
    g341: LineSegment StartX=14.9262 StartY=45.1833 StartZ=0 EndX=14.8252 EndY=45.0743 EndZ=0
    g342: LineSegment StartX=14.8252 StartY=45.0743 StartZ=0 EndX=14.725 EndY=44.9645 EndZ=0
    g343: LineSegment StartX=14.725 StartY=44.9645 StartZ=0 EndX=14.6258 EndY=44.8539 EndZ=0
    g344: LineSegment StartX=14.6258 StartY=44.8539 StartZ=0 EndX=14.5275 EndY=44.7425 EndZ=0
    g345: LineSegment StartX=14.5275 StartY=44.7425 StartZ=0 EndX=14.4301 EndY=44.6302 EndZ=0
    g346: LineSegment StartX=14.4301 StartY=44.6302 StartZ=0 EndX=14.3336 EndY=44.5172 EndZ=0
    g347: LineSegment StartX=14.3336 StartY=44.5172 StartZ=0 EndX=14.2381 EndY=44.4034 EndZ=0
    g348: LineSegment StartX=14.2381 StartY=44.4034 StartZ=0 EndX=14.1435 EndY=44.2888 EndZ=0
    g349: LineSegment StartX=14.1435 StartY=44.2888 StartZ=0 EndX=14.0499 EndY=44.1734 EndZ=0
    g350: LineSegment StartX=14.0499 StartY=44.1734 StartZ=0 EndX=13.9572 EndY=44.0572 EndZ=0
    g351: LineSegment StartX=13.9572 StartY=44.0572 StartZ=0 EndX=13.8655 EndY=43.9403 EndZ=0
    g352: LineSegment StartX=13.8655 StartY=43.9403 StartZ=0 EndX=13.7748 EndY=43.8226 EndZ=0
    g353: LineSegment StartX=13.7748 StartY=43.8226 StartZ=0 EndX=13.685 EndY=43.7042 EndZ=0
    g354: LineSegment StartX=13.685 StartY=43.7042 StartZ=0 EndX=13.5962 EndY=43.5851 EndZ=0
    g355: LineSegment StartX=13.5962 StartY=43.5851 StartZ=0 EndX=13.5084 EndY=43.4652 EndZ=0
    g356: LineSegment StartX=13.5084 StartY=43.4652 StartZ=0 EndX=13.4216 EndY=43.3446 EndZ=0
    g357: LineSegment StartX=13.4216 StartY=43.3446 StartZ=0 EndX=13.3358 EndY=43.2233 EndZ=0
    g358: LineSegment StartX=13.3358 StartY=43.2233 StartZ=0 EndX=13.251 EndY=43.1012 EndZ=0
    g359: LineSegment StartX=13.251 StartY=43.1012 StartZ=0 EndX=13.1672 EndY=42.9785 EndZ=0
    g360: LineSegment StartX=13.1672 StartY=42.9785 StartZ=0 EndX=13.0844 EndY=42.8551 EndZ=0
    g361: LineSegment StartX=13.0844 StartY=42.8551 StartZ=0 EndX=13.0027 EndY=42.731 EndZ=0
    g362: LineSegment StartX=13.0027 StartY=42.731 StartZ=0 EndX=12.9219 EndY=42.6063 EndZ=0
    g363: LineSegment StartX=12.9219 StartY=42.6063 StartZ=0 EndX=12.8422 EndY=42.4809 EndZ=0
    g364: LineSegment StartX=12.8422 StartY=42.4809 StartZ=0 EndX=12.7636 EndY=42.3548 EndZ=0
    g365: LineSegment StartX=12.7636 StartY=42.3548 StartZ=0 EndX=12.6859 EndY=42.2281 EndZ=0
    g366: LineSegment StartX=12.6859 StartY=42.2281 StartZ=0 EndX=12.6094 EndY=42.1007 EndZ=0
    g367: LineSegment StartX=12.6094 StartY=42.1007 StartZ=0 EndX=12.5339 EndY=41.9728 EndZ=0
    g368: LineSegment StartX=12.5339 StartY=41.9728 StartZ=0 EndX=12.4594 EndY=41.8442 EndZ=0
    g369: LineSegment StartX=12.4594 StartY=41.8442 StartZ=0 EndX=12.386 EndY=41.715 EndZ=0
    g370: LineSegment StartX=12.386 StartY=41.715 StartZ=0 EndX=12.3137 EndY=41.5851 EndZ=0
    g371: LineSegment StartX=12.3137 StartY=41.5851 StartZ=0 EndX=12.2424 EndY=41.4547 EndZ=0
    g372: LineSegment StartX=12.2424 StartY=41.4547 StartZ=0 EndX=12.1723 EndY=41.3238 EndZ=0
    g373: LineSegment StartX=12.1723 StartY=41.3238 StartZ=0 EndX=12.1032 EndY=41.1922 EndZ=0
    g374: LineSegment StartX=12.1032 StartY=41.1922 StartZ=0 EndX=12.0352 EndY=41.0601 EndZ=0
    g375: LineSegment StartX=12.0352 StartY=41.0601 StartZ=0 EndX=11.9683 EndY=40.9274 EndZ=0
    g376: LineSegment StartX=11.9683 StartY=40.9274 StartZ=0 EndX=11.9025 EndY=40.7942 EndZ=0
    g377: LineSegment StartX=11.9025 StartY=40.7942 StartZ=0 EndX=11.8378 EndY=40.6604 EndZ=0
    g378: LineSegment StartX=11.8378 StartY=40.6604 StartZ=0 EndX=11.7742 EndY=40.5261 EndZ=0
    g379: LineSegment StartX=11.7742 StartY=40.5261 StartZ=0 EndX=11.7117 EndY=40.3913 EndZ=0
    g380: LineSegment StartX=11.7117 StartY=40.3913 StartZ=0 EndX=11.6503 EndY=40.2559 EndZ=0
    g381: LineSegment StartX=11.6503 StartY=40.2559 StartZ=0 EndX=11.5901 EndY=40.1201 EndZ=0
    g382: LineSegment StartX=11.5901 StartY=40.1201 StartZ=0 EndX=11.5309 EndY=39.9838 EndZ=0
    g383: LineSegment StartX=11.5309 StartY=39.9838 StartZ=0 EndX=11.4729 EndY=39.847 EndZ=0
    g384: LineSegment StartX=11.4729 StartY=39.847 StartZ=0 EndX=11.4161 EndY=39.7097 EndZ=0
    g385: LineSegment StartX=11.4161 StartY=39.7097 StartZ=0 EndX=11.3603 EndY=39.5719 EndZ=0
    g386: LineSegment StartX=11.3603 StartY=39.5719 StartZ=0 EndX=11.3057 EndY=39.4337 EndZ=0
    g387: LineSegment StartX=11.3057 StartY=39.4337 StartZ=0 EndX=11.2523 EndY=39.2951 EndZ=0
    g388: LineSegment StartX=11.2523 StartY=39.2951 StartZ=0 EndX=11.2 EndY=39.156 EndZ=0
    g389: LineSegment StartX=11.2 StartY=39.156 StartZ=0 EndX=11.1488 EndY=39.0165 EndZ=0
    g390: LineSegment StartX=11.1488 StartY=39.0165 StartZ=0 EndX=11.0988 EndY=38.8765 EndZ=0
    g391: LineSegment StartX=11.0988 StartY=38.8765 StartZ=0 EndX=11.05 EndY=38.7362 EndZ=0
    g392: LineSegment StartX=11.05 StartY=38.7362 StartZ=0 EndX=11.0023 EndY=38.5955 EndZ=0
    g393: LineSegment StartX=11.0023 StartY=38.5955 StartZ=0 EndX=10.9558 EndY=38.4543 EndZ=0
    g394: LineSegment StartX=10.9558 StartY=38.4543 StartZ=0 EndX=10.9104 EndY=38.3128 EndZ=0
    g395: LineSegment StartX=10.9104 StartY=38.3128 StartZ=0 EndX=10.8662 EndY=38.171 EndZ=0
    g396: LineSegment StartX=10.8662 StartY=38.171 StartZ=0 EndX=10.8232 EndY=38.0287 EndZ=0
    g397: LineSegment StartX=10.8232 StartY=38.0287 StartZ=0 EndX=10.7814 EndY=37.8861 EndZ=0
    g398: LineSegment StartX=10.7814 StartY=37.8861 StartZ=0 EndX=10.7407 EndY=37.7432 EndZ=0
    g399: LineSegment StartX=10.7407 StartY=37.7432 StartZ=0 EndX=10.7012 EndY=37.6 EndZ=0
    ... +312 more geometry lines
  constraints (715):
    c: Coincident(g0,g1)
    c: Coincident(g1,g2)
    c: Coincident(g2,g3)
    c: Coincident(g3,g4)
    c: Coincident(g4,g5)
    c: Coincident(g5,g6)
    c: Coincident(g6,g7)
    c: Coincident(g7,g8)
    c: Coincident(g8,g9)
    c: Coincident(g9,g10)
    c: Coincident(g10,g11)
    c: Coincident(g11,g12)
    c: Coincident(g12,g13)
    c: Coincident(g13,g14)
    c: Coincident(g14,g15)
    c: Coincident(g15,g16)
    c: Coincident(g16,g17)
    c: Coincident(g17,g18)
    c: Coincident(g18,g19)
    c: Coincident(g19,g20)
    c: Coincident(g20,g21)
    c: Coincident(g21,g22)
    c: Coincident(g22,g23)
    c: Coincident(g23,g24)
    c: Coincident(g24,g25)
    c: Coincident(g25,g26)
    c: Coincident(g26,g27)
    c: Coincident(g27,g28)
    c: Coincident(g28,g29)
    c: Coincident(g29,g30)
    c: Coincident(g30,g31)
    c: Coincident(g31,g32)
    c: Coincident(g32,g33)
    c: Coincident(g33,g34)
    c: Coincident(g34,g35)
    c: Coincident(g35,g36)
    c: Coincident(g36,g37)
    c: Coincident(g37,g38)
    c: Coincident(g38,g39)
    c: Coincident(g39,g40)
    c: Coincident(g40,g41)
    c: Coincident(g41,g42)
    c: Coincident(g42,g43)
    c: Coincident(g43,g44)
    c: Coincident(g44,g45)
    c: Coincident(g45,g46)
    c: Coincident(g46,g47)
    c: Coincident(g47,g48)
    c: Coincident(g48,g49)
    c: Coincident(g49,g50)
    c: Coincident(g50,g51)
    c: Coincident(g51,g52)
    c: Coincident(g52,g53)
    c: Coincident(g53,g54)
    c: Coincident(g54,g55)
    c: Coincident(g55,g56)
    c: Coincident(g56,g57)
    c: Coincident(g57,g58)
    c: Coincident(g58,g59)
    c: Coincident(g59,g60)
    c: Coincident(g60,g61)
    c: Coincident(g61,g62)
    c: Coincident(g62,g63)
    c: Coincident(g63,g64)
    c: Coincident(g64,g65)
    c: Coincident(g65,g66)
    c: Coincident(g66,g67)
    c: Coincident(g67,g68)
    c: Coincident(g68,g69)
    c: Coincident(g69,g70)
    c: Coincident(g70,g71)
    c: Coincident(g71,g72)
    c: Coincident(g72,g73)
    c: Coincident(g73,g74)
    c: Coincident(g74,g75)
    c: Coincident(g75,g76)
    c: Coincident(g76,g77)
    c: Coincident(g77,g78)
    c: Coincident(g78,g79)
    c: Coincident(g79,g80)
    c: Coincident(g80,g81)
    c: Coincident(g81,g82)
    c: Coincident(g82,g83)
    c: Coincident(g83,g84)
    c: Coincident(g84,g85)
    c: Coincident(g85,g86)
    c: Coincident(g86,g87)
    c: Coincident(g87,g88)
    c: Coincident(g88,g89)
    c: Coincident(g89,g90)
    c: Coincident(g90,g91)
    c: Coincident(g91,g92)
    c: Coincident(g92,g93)
    c: Coincident(g93,g94)
    c: Coincident(g94,g95)
    c: Coincident(g95,g96)
    c: Coincident(g96,g97)
    c: Coincident(g97,g98)
    c: Coincident(g98,g99)
    c: Coincident(g99,g100)
    c: Coincident(g100,g101)
    c: Coincident(g101,g102)
    c: Coincident(g102,g103)
    c: Coincident(g103,g104)
    c: Coincident(g104,g105)
    c: Coincident(g105,g106)
    c: Coincident(g106,g107)
    c: Coincident(g107,g108)
    c: Coincident(g108,g109)
    c: Coincident(g109,g110)
    c: Coincident(g110,g111)
    c: Horizontal(g111)
    c: Coincident(g111,g112)
    c: Coincident(g112,g113)
    c: Coincident(g113,g114)
    c: Coincident(g114,g115)
    c: Coincident(g115,g116)
    c: Coincident(g116,g117)
    c: Coincident(g117,g118)
    c: Coincident(g118,g119)
    c: Coincident(g119,g120)
    c: Coincident(g120,g121)
    c: Coincident(g121,g122)
    c: Coincident(g122,g123)
    c: Coincident(g123,g124)
    c: Coincident(g124,g125)
    c: Coincident(g125,g126)
    c: Coincident(g126,g127)
    c: Coincident(g127,g128)
    c: Coincident(g128,g129)
    c: Coincident(g129,g130)
    c: Coincident(g130,g131)
    c: Coincident(g131,g132)
    c: Coincident(g132,g133)
    c: Coincident(g133,g134)
    c: Coincident(g134,g135)
    c: Coincident(g135,g136)
    c: Coincident(g136,g137)
    c: Coincident(g137,g138)
    c: Coincident(g138,g139)
    c: Coincident(g139,g140)
    c: Coincident(g140,g141)
    c: Coincident(g141,g142)
    c: Coincident(g142,g143)
    c: Coincident(g143,g144)
    c: Coincident(g144,g145)
    c: Coincident(g145,g146)
    c: Coincident(g146,g147)
    c: Coincident(g147,g148)
    c: Coincident(g148,g149)
    c: Coincident(g149,g150)
    c: Coincident(g150,g151)
    c: Coincident(g151,g152)
    c: Coincident(g152,g153)
    c: Coincident(g153,g154)
    c: Coincident(g154,g155)
    c: Coincident(g155,g156)
    c: Coincident(g156,g157)
    c: Coincident(g157,g158)
    c: Coincident(g158,g159)
    c: Coincident(g159,g160)
    c: Coincident(g160,g161)
    c: Coincident(g161,g162)
    c: Coincident(g162,g163)
    c: Coincident(g163,g164)
    c: Coincident(g164,g165)
    c: Coincident(g165,g166)
    c: Coincident(g166,g167)
    c: Coincident(g167,g168)
    c: Coincident(g168,g169)
    c: Coincident(g169,g170)
    c: Coincident(g170,g171)
    c: Coincident(g171,g172)
    c: Coincident(g172,g173)
    c: Coincident(g173,g174)
    c: Coincident(g174,g175)
    c: Coincident(g175,g176)
    c: Coincident(g176,g177)
    c: Coincident(g177,g178)
    c: Coincident(g178,g179)
    c: Coincident(g179,g180)
    c: Coincident(g180,g181)
    c: Coincident(g181,g182)
    c: Coincident(g182,g183)
    c: Coincident(g183,g184)
    c: Coincident(g184,g185)
    c: Coincident(g185,g186)
    c: Coincident(g186,g187)
    c: Coincident(g187,g188)
    c: Coincident(g188,g189)
    c: Coincident(g189,g190)
    c: Coincident(g190,g191)
    c: Coincident(g191,g192)
    c: Coincident(g192,g193)
    c: Coincident(g193,g194)
    c: Coincident(g194,g195)
    c: Coincident(g195,g196)
    c: Coincident(g196,g197)
    c: Coincident(g197,g198)
    c: Coincident(g198,g199)
    c: Coincident(g199,g200)
    c: Coincident(g200,g201)
    c: Coincident(g201,g202)
    c: Coincident(g202,g203)
    c: Coincident(g203,g204)
    c: Coincident(g204,g205)
    c: Coincident(g205,g206)
    c: Coincident(g206,g207)
    c: Coincident(g207,g208)
    c: Coincident(g208,g209)
    c: Coincident(g209,g210)
    c: Coincident(g210,g211)
    c: Coincident(g211,g212)
    c: Coincident(g212,g213)
    c: Coincident(g213,g214)
    c: Coincident(g214,g215)
    c: Coincident(g215,g216)
    c: Coincident(g216,g217)
    c: Coincident(g217,g218)
    c: Coincident(g218,g219)
    c: Coincident(g219,g220)
    c: Coincident(g220,g221)
    c: Coincident(g221,g222)
    c: Coincident(g222,g223)
    c: Coincident(g223,g224)
    c: Coincident(g224,g225)
    c: Coincident(g225,g226)
    c: Coincident(g226,g227)
    c: Coincident(g227,g228)
    c: Coincident(g228,g229)
    c: Coincident(g229,g230)
    c: Coincident(g230,g231)
    c: Coincident(g231,g232)
    c: Coincident(g232,g233)
    c: Coincident(g233,g234)
    c: Coincident(g234,g235)
    c: Coincident(g235,g236)
    c: Coincident(g236,g237)
    c: Coincident(g237,g238)
    c: Coincident(g238,g239)
    c: Coincident(g239,g240)
    c: Coincident(g240,g241)
    c: Coincident(g241,g242)
    c: Coincident(g242,g243)
    c: Coincident(g243,g244)
    c: Coincident(g244,g245)
    c: Coincident(g245,g246)
    c: Coincident(g246,g247)
    c: Coincident(g247,g248)
    c: Coincident(g248,g249)
    c: Coincident(g249,g250)
    c: Coincident(g250,g251)
    c: Coincident(g251,g252)
    c: Coincident(g252,g253)
    c: Coincident(g253,g254)
    c: Coincident(g254,g255)
    c: Coincident(g255,g256)
    c: Coincident(g256,g257)
    c: Coincident(g257,g258)
    c: Coincident(g258,g259)
    c: Coincident(g259,g260)
    c: Coincident(g260,g261)
    c: Coincident(g261,g262)
    c: Coincident(g262,g263)
    c: Coincident(g263,g264)
    c: Coincident(g264,g265)
    c: Coincident(g265,g266)
    c: Coincident(g266,g267)
    c: Coincident(g267,g268)
    c: Coincident(g268,g269)
    c: Coincident(g269,g270)
    c: Coincident(g270,g271)
    c: Coincident(g271,g272)
    c: Coincident(g272,g273)
    c: Coincident(g273,g274)
    c: Coincident(g274,g275)
    c: Coincident(g275,g276)
    c: Coincident(g276,g277)
    c: Coincident(g277,g278)
    c: Coincident(g278,g279)
    c: Coincident(g279,g280)
    c: Coincident(g280,g281)
    c: Coincident(g281,g282)
    c: Coincident(g282,g283)
    c: Coincident(g283,g284)
    c: Coincident(g284,g285)
    c: Coincident(g285,g286)
    c: Coincident(g286,g287)
    c: Coincident(g287,g288)
    c: Coincident(g288,g289)
    c: Coincident(g289,g290)
    c: Coincident(g290,g291)
    c: Coincident(g291,g292)
    c: Coincident(g292,g293)
    c: Coincident(g293,g294)
    c: Coincident(g294,g295)
    c: Coincident(g295,g296)
    c: Coincident(g296,g297)
    c: Coincident(g297,g298)
    c: Coincident(g298,g299)
    c: Coincident(g299,g300)
    c: Coincident(g300,g301)
    c: Coincident(g301,g302)
    c: Coincident(g302,g303)
    c: Coincident(g303,g304)
    c: Coincident(g304,g305)
    c: Coincident(g305,g306)
    c: Coincident(g306,g307)
    c: Coincident(g307,g308)
    c: Coincident(g308,g309)
    c: Coincident(g309,g310)
    c: Coincident(g310,g311)
    c: Coincident(g311,g312)
    c: Coincident(g312,g313)
    c: Coincident(g313,g314)
    c: Coincident(g314,g315)
    c: Coincident(g315,g316)
    c: Coincident(g316,g317)
    c: Coincident(g317,g318)
    c: Coincident(g318,g319)
    c: Coincident(g319,g320)
    c: Coincident(g320,g321)
    c: Coincident(g321,g322)
    c: Coincident(g322,g323)
    c: Coincident(g323,g324)
    c: Coincident(g324,g325)
    c: Coincident(g325,g326)
    c: Coincident(g326,g327)
    c: Coincident(g327,g328)
    c: Coincident(g328,g329)
    c: Coincident(g329,g330)
    c: Coincident(g330,g331)
    c: Coincident(g331,g332)
    c: Coincident(g332,g333)
    c: Coincident(g333,g334)
    c: Coincident(g334,g335)
    c: Coincident(g335,g336)
    c: Coincident(g336,g337)
    c: Coincident(g337,g338)
    c: Coincident(g338,g339)
    c: Coincident(g339,g340)
    c: Coincident(g340,g341)
    c: Coincident(g341,g342)
    c: Coincident(g342,g343)
    c: Coincident(g343,g344)
    c: Coincident(g344,g345)
    c: Coincident(g345,g346)
    c: Coincident(g346,g347)
    c: Coincident(g347,g348)
    c: Coincident(g348,g349)
    c: Coincident(g349,g350)
    c: Coincident(g350,g351)
    c: Coincident(g351,g352)
    c: Coincident(g352,g353)
    c: Coincident(g353,g354)
    c: Coincident(g354,g355)
    c: Coincident(g355,g356)
    c: Coincident(g356,g357)
    c: Coincident(g357,g358)
    c: Coincident(g358,g359)
    c: Coincident(g359,g360)
    c: Coincident(g360,g361)
    c: Coincident(g361,g362)
    c: Coincident(g362,g363)
    c: Coincident(g363,g364)
    c: Coincident(g364,g365)
    c: Coincident(g365,g366)
    c: Coincident(g366,g367)
    c: Coincident(g367,g368)
    c: Coincident(g368,g369)
    c: Coincident(g369,g370)
    c: Coincident(g370,g371)
    c: Coincident(g371,g372)
    c: Coincident(g372,g373)
    c: Coincident(g373,g374)
    c: Coincident(g374,g375)
    c: Coincident(g375,g376)
    c: Coincident(g376,g377)
    c: Coincident(g377,g378)
    c: Coincident(g378,g379)
    c: Coincident(g379,g380)
    c: Coincident(g380,g381)
    c: Coincident(g381,g382)
    c: Coincident(g382,g383)
    c: Coincident(g383,g384)
    c: Coincident(g384,g385)
    c: Coincident(g385,g386)
    c: Coincident(g386,g387)
    c: Coincident(g387,g388)
    c: Coincident(g388,g389)
    c: Coincident(g389,g390)
    c: Coincident(g390,g391)
    c: Coincident(g391,g392)
    c: Coincident(g392,g393)
    c: Coincident(g393,g394)
    c: Coincident(g394,g395)
    c: Coincident(g395,g396)
    c: Coincident(g396,g397)
    c: Coincident(g397,g398)
    c: Coincident(g398,g399)
    c: Coincident(g399,g400)
    c: Coincident(g400,g401)
    c: Coincident(g401,g402)
    c: Coincident(g402,g403)
    c: Coincident(g403,g404)
    c: Coincident(g404,g405)
    c: Coincident(g405,g406)
    c: Coincident(g406,g407)
    c: Coincident(g407,g408)
    c: Coincident(g408,g409)
    c: Coincident(g409,g410)
    c: Coincident(g410,g411)
    c: Coincident(g411,g412)
    c: Coincident(g412,g413)
    c: Coincident(g413,g414)
    c: Coincident(g414,g415)
    c: Coincident(g415,g416)
    c: Coincident(g416,g417)
    c: Coincident(g417,g418)
    c: Coincident(g418,g419)
    c: Coincident(g419,g420)
    c: Coincident(g420,g421)
    c: Coincident(g421,g422)
    c: Coincident(g422,g423)
    c: Coincident(g423,g424)
    c: Coincident(g424,g425)
    c: Coincident(g425,g426)
    c: Coincident(g426,g427)
    c: Coincident(g427,g428)
    c: Coincident(g428,g429)
    c: Coincident(g429,g430)
    c: Coincident(g430,g431)
    c: Coincident(g431,g432)
    c: Coincident(g432,g433)
    c: Coincident(g433,g434)
    c: Coincident(g434,g435)
    c: Coincident(g435,g436)
    c: Coincident(g436,g437)
    c: Coincident(g437,g438)
    c: Coincident(g438,g439)
    c: Coincident(g439,g440)
    c: Coincident(g440,g441)
    c: Coincident(g441,g442)
    c: Coincident(g442,g443)
    c: Coincident(g443,g444)
    c: Coincident(g444,g445)
    c: Coincident(g445,g446)
    c: Coincident(g446,g447)
    c: Coincident(g447,g448)
    c: Coincident(g448,g449)
    c: Coincident(g449,g450)
    c: Coincident(g450,g451)
    c: Coincident(g451,g452)
    c: Coincident(g452,g453)
    c: Coincident(g453,g454)
    c: Coincident(g454,g455)
    c: Coincident(g455,g456)
    c: Coincident(g456,g457)
    c: Coincident(g457,g458)
    c: Coincident(g458,g459)
    c: Coincident(g459,g460)
    c: Coincident(g460,g461)
    c: Coincident(g461,g462)
    c: Coincident(g462,g463)
    c: Coincident(g463,g464)
    c: Coincident(g464,g465)
    c: Coincident(g465,g466)
    c: Coincident(g466,g467)
    c: Coincident(g467,g468)
    c: Coincident(g468,g469)
    c: Coincident(g469,g470)
    c: Coincident(g470,g471)
    c: Coincident(g471,g472)
    c: Coincident(g472,g473)
    c: Coincident(g473,g474)
    c: Coincident(g474,g475)
    c: Coincident(g475,g476)
    c: Coincident(g476,g477)
    c: Coincident(g477,g478)
    c: Coincident(g478,g479)
    c: Coincident(g479,g480)
    c: Coincident(g480,g481)
    c: Coincident(g481,g482)
    c: Coincident(g482,g483)
    c: Coincident(g483,g484)
    c: Coincident(g484,g485)
    c: Coincident(g485,g486)
    c: Coincident(g486,g487)
    c: Coincident(g487,g488)
    c: Coincident(g488,g489)
    c: Coincident(g489,g490)
    c: Coincident(g490,g491)
    c: Coincident(g491,g492)
    c: Coincident(g492,g493)
    c: Coincident(g493,g494)
    c: Coincident(g494,g495)
    c: Coincident(g495,g496)
    c: Coincident(g496,g497)
    c: Coincident(g497,g498)
    c: Coincident(g498,g499)
    c: Coincident(g499,g500)
    c: Coincident(g500,g501)
    c: Coincident(g501,g502)
    c: Coincident(g502,g503)
    c: Coincident(g503,g504)
    c: Coincident(g504,g505)
    c: Coincident(g505,g506)
    c: Coincident(g506,g507)
    c: Coincident(g507,g508)
    c: Coincident(g508,g509)
    c: Coincident(g509,g510)
    c: Coincident(g510,g511)
    c: Coincident(g511,g512)
    c: Coincident(g512,g513)
    c: Coincident(g513,g514)
    c: Coincident(g514,g515)
    c: Coincident(g515,g516)
    c: Coincident(g516,g517)
    c: Coincident(g517,g518)
    c: Coincident(g518,g519)
    c: Coincident(g519,g520)
    c: Coincident(g520,g521)
    c: Coincident(g521,g522)
    c: Coincident(g522,g523)
    c: Coincident(g523,g524)
    c: Coincident(g524,g525)
    c: Coincident(g525,g526)
    c: Coincident(g526,g527)
    c: Coincident(g527,g528)
    c: Coincident(g528,g529)
    c: Coincident(g529,g530)
    c: Coincident(g530,g531)
    c: Coincident(g531,g532)
    c: Coincident(g532,g533)
    c: Coincident(g533,g534)
    c: Coincident(g534,g535)
    c: Coincident(g535,g536)
    c: Coincident(g536,g537)
    c: Coincident(g537,g538)
    c: Coincident(g538,g539)
    c: Coincident(g539,g540)
    c: Coincident(g540,g541)
    c: Coincident(g541,g542)
    c: Coincident(g542,g543)
    c: Coincident(g543,g544)
    c: Coincident(g544,g545)
    c: Coincident(g545,g546)
    c: Coincident(g546,g547)
    c: Coincident(g547,g548)
    c: Coincident(g548,g549)
    c: Coincident(g549,g550)
    c: Coincident(g550,g551)
    c: Coincident(g551,g552)
    c: Coincident(g552,g553)
    c: Coincident(g553,g554)
    c: Coincident(g554,g555)
    c: Coincident(g555,g556)
    c: Coincident(g556,g557)
    c: Coincident(g557,g558)
    c: Coincident(g558,g559)
    c: Coincident(g559,g560)
    c: Coincident(g560,g561)
    c: Coincident(g561,g562)
    c: Coincident(g562,g563)
    c: Coincident(g563,g564)
    c: Coincident(g564,g565)
    c: Coincident(g565,g566)
    c: Coincident(g566,g567)
    c: Coincident(g567,g568)
    c: Coincident(g568,g569)
    c: Coincident(g569,g570)
    c: Coincident(g570,g571)
    c: Coincident(g571,g572)
    c: Coincident(g572,g573)
    c: Coincident(g573,g574)
    c: Coincident(g574,g575)
    c: Coincident(g575,g576)
    c: Coincident(g576,g577)
    c: Coincident(g577,g578)
    c: Coincident(g578,g579)
    c: Coincident(g579,g580)
    c: Coincident(g580,g581)
    c: Coincident(g581,g582)
    c: Coincident(g582,g583)
    c: Coincident(g583,g584)
    c: Coincident(g584,g585)
    c: Coincident(g585,g586)
    c: Coincident(g586,g587)
    c: Coincident(g587,g588)
    c: Coincident(g588,g589)
    c: Coincident(g589,g590)
    c: Coincident(g590,g591)
    c: Coincident(g591,g592)
    c: Coincident(g592,g593)
    c: Coincident(g593,g594)
    c: Coincident(g594,g595)
    c: Coincident(g595,g596)
    c: Coincident(g596,g597)
    c: Coincident(g597,g598)
    c: Coincident(g598,g599)
    c: Coincident(g599,g600)
    c: Coincident(g600,g601)
    c: Coincident(g601,g602)
    c: Coincident(g602,g603)
    c: Coincident(g603,g604)
    c: Coincident(g604,g605)
    c: Coincident(g605,g606)
    c: Coincident(g606,g607)
    c: Coincident(g607,g608)
    c: Coincident(g608,g609)
    c: Coincident(g609,g610)
    c: Coincident(g610,g611)
    c: Coincident(g611,g612)
    c: Coincident(g612,g613)
    c: Coincident(g613,g614)
    c: Coincident(g614,g615)
    c: Coincident(g615,g616)
    c: Coincident(g616,g617)
    c: Coincident(g617,g618)
    c: Coincident(g618,g619)
    c: Coincident(g619,g620)
    c: Coincident(g620,g621)
    c: Coincident(g621,g622)
    c: Coincident(g622,g623)
    c: Coincident(g623,g624)
    c: Coincident(g624,g625)
    c: Coincident(g625,g626)
    c: Coincident(g626,g627)
    c: Coincident(g627,g628)
    c: Coincident(g628,g629)
    c: Coincident(g629,g630)
    c: Coincident(g630,g631)
    c: Coincident(g631,g632)
    c: Coincident(g632,g633)
    c: Coincident(g633,g634)
    c: Coincident(g634,g635)
    c: Coincident(g635,g636)
    c: Coincident(g636,g637)
    c: Coincident(g637,g638)
    c: Coincident(g638,g639)
    c: Coincident(g639,g640)
    c: Coincident(g640,g641)
    c: Coincident(g641,g642)
    c: Coincident(g642,g643)
    c: Coincident(g643,g644)
    c: Coincident(g644,g645)
    c: Coincident(g645,g646)
    c: Coincident(g646,g647)
    c: Coincident(g647,g648)
    c: Coincident(g648,g649)
    c: Coincident(g649,g650)
    c: Coincident(g650,g651)
    c: Coincident(g651,g652)
    c: Coincident(g652,g653)
    c: Coincident(g653,g654)
    c: Coincident(g654,g655)
    c: Coincident(g655,g656)
    c: Coincident(g656,g657)
    c: Coincident(g657,g658)
    c: Coincident(g658,g659)
    c: Coincident(g659,g660)
    c: Coincident(g660,g661)
    c: Coincident(g661,g662)
    c: Coincident(g662,g663)
    c: Coincident(g663,g664)
    c: Coincident(g664,g665)
    c: Coincident(g665,g666)
    c: Coincident(g666,g667)
    c: Coincident(g667,g668)
    c: Coincident(g668,g669)
    c: Coincident(g669,g670)
    c: Coincident(g670,g671)
    c: Coincident(g671,g672)
    c: Coincident(g672,g673)
    c: Coincident(g673,g674)
    c: Coincident(g674,g675)
    c: Coincident(g675,g676)
    c: Coincident(g676,g677)
    c: Coincident(g677,g678)
    c: Coincident(g678,g679)
    c: Coincident(g679,g680)
    c: Coincident(g680,g681)
    c: Coincident(g681,g682)
    c: Coincident(g682,g683)
    c: Coincident(g683,g684)
    c: Coincident(g684,g685)
    c: Coincident(g685,g686)
    c: Coincident(g686,g687)
    c: Coincident(g687,g688)
    c: Coincident(g688,g689)
    c: Coincident(g689,g690)
    c: Coincident(g690,g691)
    c: Coincident(g691,g692)
    c: Coincident(g692,g693)
    c: Coincident(g693,g694)
    c: Coincident(g694,g695)
    c: Coincident(g695,g696)
    c: Coincident(g696,g697)
    c: Coincident(g697,g698)
    c: Coincident(g698,g699)
    c: Coincident(g699,g700)
    c: Coincident(g700,g701)
    c: Coincident(g701,g702)
    c: Coincident(g702,g703)
    c: Coincident(g703,g704)
    c: Coincident(g704,g705)
    c: Coincident(g705,g706)
    c: Coincident(g706,g707)
    c: Coincident(g707,g708)
    c: Coincident(g708,g709)
    c: Coincident(g709,g710)
    c: Coincident(g710,g0)
    c: Radius(g711) = 4
    c: DistanceX(g-1,g711) = 30.34
    c: DistanceY(g-1,g711) = 36.02
FEATURE [PartDesign::Pad] Pad
  Direction = (1,1,1)
  Length = 9
  Length2 = 100
  Profile = -> Sketch002
  Type = 0
FEATURE [PartDesign::Body] Body
  Group = -> [Sketch002,Pad]
  Origin = -> Origin
  Tip = -> Pad
FEATURE [App::FeaturePython] SetupSheet  # Path/CAM operation (typed FeaturePython)
  ClearanceHeightExpression = OpStockZMax+SetupSheet.ClearanceHeightOffset
  ClearanceHeightOffset = 5
  CoolantMode = 0
  CoolantModes = None | Flood | Mist
  FinalDepthExpression = OpFinalDepth
  HorizRapid = 0
  SafeHeightExpression = OpStockZMax+SetupSheet.SafeHeightOffset
  SafeHeightOffset = 3
  StartDepthExpression = OpStartDepth
  StepDownExpression = OpToolDiameter
  VertRapid = 0
FEATURE [Part::FeaturePython] Clone  label="Model-Body"  # Draft clone (typed FeaturePython)
  AttacherType = Attacher::AttachEngine3D
  Fuse = false
  Objects = -> [Body]
  PathResource = Model
  Placement = pos=(-9,-9,-9) rot=(0,0,1;0rad)
  Scale = (1,1,1)
FEATURE [App::DocumentObjectGroup] Model
  Group = -> [Clone]
FEATURE [Part::FeaturePython] ToolBit  label="Endmill"  # Path/CAM toolbit (typed FeaturePython)
  BitPropertyNames = Chipload | CuttingEdgeHeight | Diameter | Flutes | Length | Material | ShankDiameter
  BitShape = /Volumes/SSD/Applications/FreeCAD_0.19-24276.app/Contents/Resources/Mod/Path/Tools/Shape/endmill.fcstd
  Chipload = 0
  CuttingEdgeHeight = 30
  Diameter = 6
  Flutes = 0
  Length = 50
  Material = 0
  ShankDiameter = 3
  ShapeName = endmill
FEATURE [Path::FeaturePython] TC__Default_Tool  label="TC: Default Tool"  # Path/CAM operation (typed FeaturePython)
  HorizFeed = 0
  HorizRapid = 0
  SpindleDir = 0
  SpindleSpeed = 0
  Tool = -> ToolBit
  ToolNumber = 1
  VertFeed = 0
  VertRapid = 0
  expr: HorizRapid = SetupSheet.HorizRapid
  expr: VertRapid = SetupSheet.VertRapid
FEATURE [App::DocumentObjectGroup] Tools
  Group = -> [TC__Default_Tool]
FEATURE [Part::FeaturePython] Stock  # WARN: FeaturePython — macro-defined, semantics opaque (R4)
  Base = -> Model
  ExtXneg = 1
  ExtXpos = 1
  ExtYneg = 1
  ExtYpos = 1
  ExtZneg = 0
  ExtZpos = 0
  Placement = pos=(1,1,-9) rot=(0,0,1;0rad)
  StockType = FromBase
FEATURE [Path::FeaturePython] Profile  # Path/CAM operation (typed FeaturePython)
  Active = true
  AreaParams:
    Tolerance = 1e-07
    FitArcs = True
    Simplify = False
    CleanDistance = 0.0
    Accuracy = 0.01
    Unit = 1.0
    MinArcPoints = 4
    MaxArcPoints = 100
    ClipperScale = 10000000.0
    Fill = 0
    Coplanar = 0
    Reorient = True
    Outline = False
    Explode = False
    OpenMode = 0
    Deflection = 0.01
    SubjectFill = 0
    ClipFill = 0
    Offset = 3.0
    ExtraPass = 0
    Stepover = 0.0
    LastStepover = 0.0
    JoinType = 0
    EndType = 0
    MiterLimit = 2.0
    RoundPrecision = 0.0
    PocketMode = 0
    ToolRadius = 1.0
    PocketExtraOffset = 0.0
    PocketStepover = 0.0
    PocketLastStepover = 0.0
    FromCenter = False
    Angle = 45.0
    AngleShift = 0.0
    Shift = 0.0
    Thicken = False
    SectionCount = -1
    Stepdown = 1.0
    SectionOffset = 0.0
    SectionTolerance = 1e-06
    SectionMode = 2
    Project = False
  AttemptInverseAngle = true
  Base = -> [Clone]
  ClearanceHeight = 5
  CoolantMode = None
  CycleTime = Cycletime Error
  Direction = 1
  EnableRotation = 0
  FinalDepth = -9
  HandleMultipleFeatures = 0
  InverseAngle = false
  JoinType = 0
  LimitDepthToFace = true
  MiterLimit = 0.1
  OffsetExtra = 0
  OpFinalDepth = -9
  OpStartDepth = 0
  OpStockZMax = 0
  OpStockZMin = -9
  OpToolDiameter = 6
  PathParams = {'orientation': 0, 'feedrate': 0.0, 'feedrate_v': 0.0, 'verbose': True, 'resume_height': 3.0, 'retraction': 5.0, 'return_end': True, 'preamble': False, 'start': Vector (0.0, 0.0, 0.0)}
  ReverseDirection = false
  SafeHeight = 3
  Side = 0
  StartDepth = 0
  StartPoint = (0,0,0)
  StepDown = 3
  ToolController = -> TC__Default_Tool
  UseComp = true
  UseStartPoint = true
  processCircles = false
  processHoles = false
  processPerimeter = true
  expr: ClearanceHeight = OpStockZMax + SetupSheet.ClearanceHeightOffset
  expr: SafeHeight = OpStockZMax + SetupSheet.SafeHeightOffset
  expr: StepDown = 3
  expr: FinalDepth = OpFinalDepth
  expr: StartDepth = OpStartDepth
FEATURE [Path::FeaturePython] DressupTag  # Path/CAM operation (typed FeaturePython)
  Angle = 45
  Base = -> Profile
  Height = 1.5
  Positions = (4) [(97.2059,36.0809,0),(47.0294,43.097,0),(9.61009,2.29758,0),(129.901,15.3005,0)]
  Radius = 0
  SegmentationFactor = 50
  Width = 10.14
FEATURE [Path::FeaturePython] Pocket_Shape  # Path/CAM operation (typed FeaturePython)
  Active = true
  AreaParams:
    Tolerance = 1e-07
    FitArcs = True
    Simplify = False
    CleanDistance = 0.0
    Accuracy = 0.01
    Unit = 1.0
    MinArcPoints = 4
    MaxArcPoints = 100
    ClipperScale = 10000000.0
    Fill = 0
    Coplanar = 0
    Reorient = True
    Outline = False
    Explode = False
    OpenMode = 0
    Deflection = 0.01
    SubjectFill = 0
    ClipFill = 0
    Offset = 0.0
    ExtraPass = 0
    Stepover = 0.0
    LastStepover = 0.0
    JoinType = 0
    EndType = 0
    MiterLimit = 2.0
    RoundPrecision = 0.0
    PocketMode = 1
    ToolRadius = 3.0
    PocketExtraOffset = 0.0
    PocketStepover = 6.0
    PocketLastStepover = 0.0
    FromCenter = True
    Angle = 45.0
    AngleShift = 0.0
    Shift = 0.0
    Thicken = False
    SectionCount = -1
    Stepdown = 1.0
    SectionOffset = 0.0
    SectionTolerance = 1e-06
    SectionMode = 2
    Project = False
  AttemptInverseAngle = true
  Base = -> [Clone]
  ClearanceHeight = 5
  CoolantMode = None
  CutMode = 0
  CycleTime = Cycletime Error
  EnableRotation = 0
  ExtensionCorners = true
  ExtensionLengthDefault = 3
  ExtraOffset = 0
  FinalDepth = -9
  FinishDepth = 0
  InverseAngle = false
  KeepToolDown = false
  LimitDepthToFace = true
  MinTravel = false
  OffsetPattern = 0
  OpFinalDepth = -9
  OpStartDepth = 0
  OpStockZMax = 0
  OpStockZMin = -9
  OpToolDiameter = 6
  PathParams = {'orientation': 1, 'feedrate': 0.0, 'feedrate_v': 0.0, 'verbose': True, 'resume_height': 3.0, 'retraction': 5.0, 'return_end': True, 'preamble': False}
  ReverseDirection = false
  SafeHeight = 3
  StartAt = 0
  StartDepth = 0
  StartPoint = (0,0,0)
  StepDown = 3
  StepOver = 100
  ToolController = -> TC__Default_Tool
  UseOutline = false
  UseStartPoint = false
  ZigZagAngle = 45
  expr: ExtensionLengthDefault = OpToolDiameter / 2
  expr: ClearanceHeight = OpStockZMax + SetupSheet.ClearanceHeightOffset
  expr: SafeHeight = OpStockZMax + SetupSheet.SafeHeightOffset
  expr: StepDown = 3
  expr: FinalDepth = OpFinalDepth
  expr: StartDepth = OpStartDepth
FEATURE [Path::FeatureCompoundPython] Operations  # Path/CAM operation (typed FeaturePython)
  Group = -> [DressupTag,Pocket_Shape]
  UsePlacements = false
FEATURE [Path::FeaturePython] Job  # Path/CAM operation (typed FeaturePython)
  CycleTime = 00:00:00
  Fixtures = G54
  GeometryTolerance = 0.01
  LastPostProcessDate = 2021-04-11 22:04:26.568162
  LastPostProcessOutput = /Volumes/SSD/Dev/CNC/MiscCNC/Coinceur2.gcode
  Model = -> Model
  Operations = -> Operations
  OrderOutputBy = 0
  PostProcessor = 1
  PostProcessorOutputFile = /Volumes/SSD/Dev/CNC/MiscCNC/Coinceur2.gcode
  SetupSheet = -> SetupSheet
  SplitOutput = false
  Stock = -> Stock
  Tools = -> Tools
FEATURE [Mesh::FeaturePython] CutMaterial  # WARN: FeaturePython — macro-defined, semantics opaque (R4)
